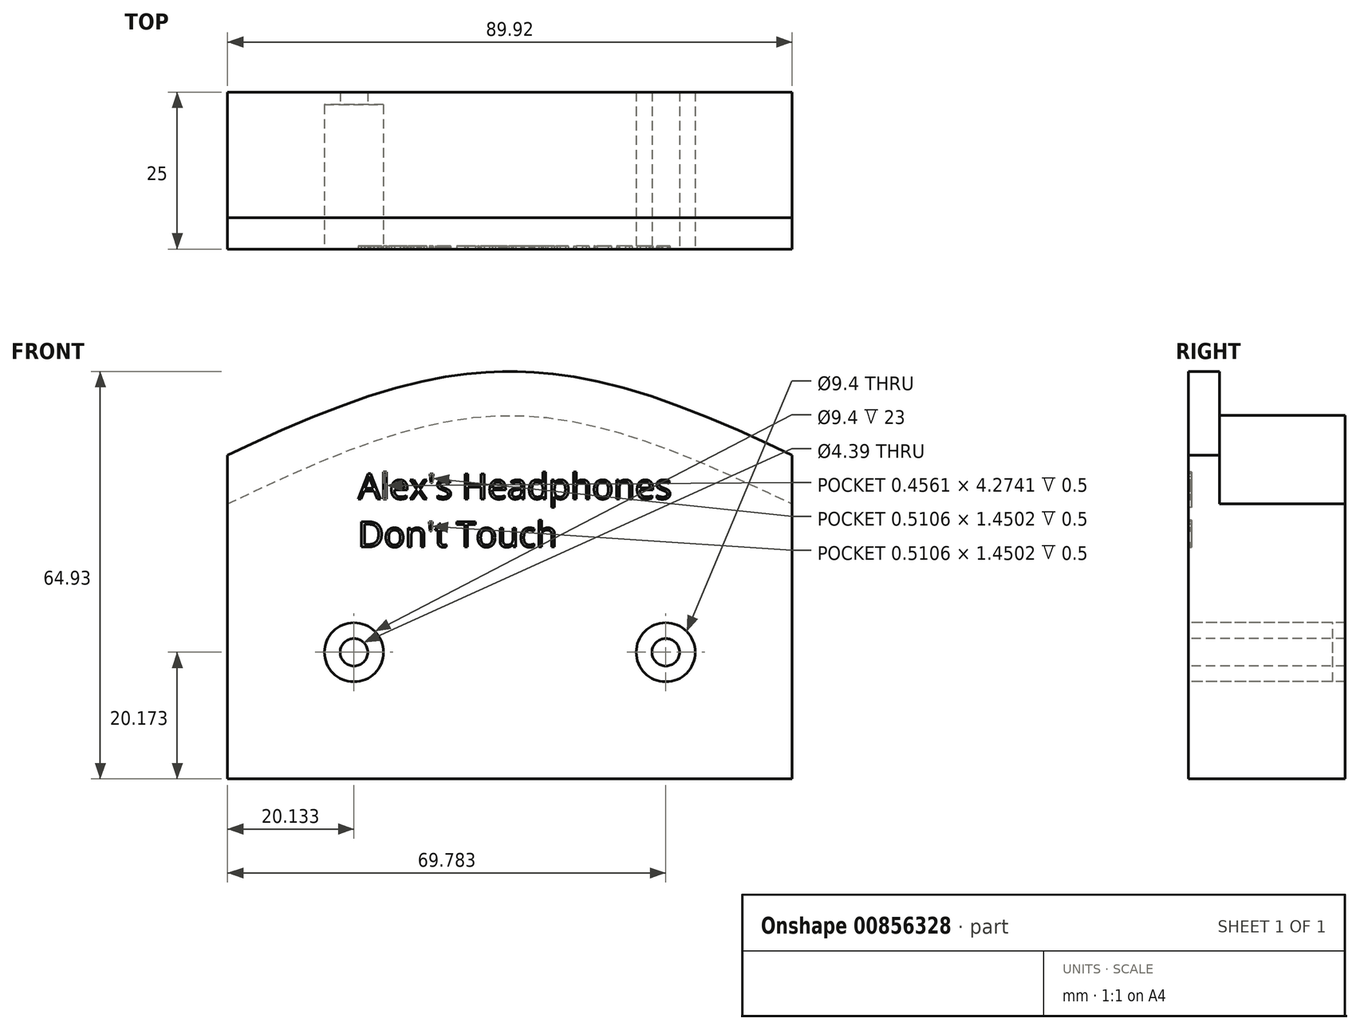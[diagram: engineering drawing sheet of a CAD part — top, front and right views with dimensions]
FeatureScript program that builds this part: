
annotation { "Feature Type Name" : "Feature", "Feature Type Description" : "" }
export const myFeature = defineFeature(function(context is Context, id is Id, definition is map)
    precondition{}
    {
        {
            var Q0;
            Q0=qCreatedBy(makeId("Front.planeOp"),FACE);
            var sketch = newSketch(context, id + "F0", { "sketchPlane" : qUnion([Q0])});
            skLineSegment(sketch, "E0.bottom", {"start": v(0, 0) * mm, "end": v(89.92, 0) * mm});
            skLineSegment(sketch, "E0.top", {"start": v(0, 43.82) * mm, "end": v(89.92, 43.82) * mm});
            skLineSegment(sketch, "E0.left", {"start": v(0, 0) * mm, "end": v(0, 43.82) * mm});
            skLineSegment(sketch, "E0.right", {"start": v(89.92, 0) * mm, "end": v(89.92, 43.82) * mm});
            skPoint(sketch, "E1.1.internal.snap0", {"position": v(44.96, 43.82) * mm});
            skFitSpline(sketch, "E1", {"points": [v(0, 43.82) * mm, v(44.96, 57.92) * mm, v(89.92, 43.82) * mm], "startDerivative": vector(89.92, 42.31) * mm, "endDerivative": vector(89.92, -42.31) * mm});
            skSolve(sketch);
        }
        {
            var Q0;
            Q0=makeQuery(id+"F0.imprint","IMPRINT",FACE,{"disambiguationData":[TD([[makeQuery(id+"F0.imprint","IMPRINT",EDGE,{"derivedFrom":sQuery(id+"F0.wireOp",EDGE,"E0.bottom")}),1.0]])]});
            var Q1;
            Q1=makeQuery(id+"F0.imprint","IMPRINT",FACE,{"disambiguationData":[TD([[makeQuery(id+"F0.imprint","IMPRINT",EDGE,{"derivedFrom":sQuery(id+"F0.wireOp",EDGE,"E0.top")}),1.0]])]});
            extrude(context, id + "F1", {"entities" : qUnion([Q0, Q1]), "depth" : 25 * mm, "offsetDistance" : 25 * mm});
        }
        {
            var Q0;
            Q0=makeQuery(id+"F1.opExtrude","CAP_FACE",FACE,{"disambiguationData":[OSD([sQuery(id+"F0.wireOp",EDGE,"E0.bottom"),sQuery(id+"F0.wireOp",EDGE,"E0.left"),sQuery(id+"F0.wireOp",EDGE,"E0.right"),sQuery(id+"F0.wireOp",EDGE,"E1")])],"isStart":false});
            var sketch = newSketch(context, id + "F2", { "sketchPlane" : qUnion([Q0])});
            skFitSpline(sketch, "E2.0", {"points": [v(-2.98, 50.15) * mm, v(0.77, 51.91) * mm, v(6.46, 54.6) * mm, v(14.22, 57.9) * mm, v(20.13, 60.17) * mm, v(26.15, 62.11) * mm, v(31.26, 63.4) * mm, v(35.42, 64.16) * mm, v(38.57, 64.59) * mm, v(41.22, 64.81) * mm, v(43.35, 64.9) * mm, v(44.96, 64.93) * mm, v(46.57, 64.9) * mm, v(48.7, 64.81) * mm, v(51.35, 64.59) * mm, v(54.5, 64.16) * mm, v(58.65, 63.4) * mm, v(63.77, 62.11) * mm, v(69.78, 60.17) * mm, v(75.7, 57.9) * mm, v(83.46, 54.6) * mm, v(89.15, 51.91) * mm, v(92.9, 50.15) * mm]});
            skLineSegment(sketch, "E3", {"start": v(0, 43.82) * mm, "end": v(0, 51.55) * mm});
            skLineSegment(sketch, "E4", {"start": v(89.92, 43.82) * mm, "end": v(89.92, 51.55) * mm});
            skSolve(sketch);
        }
        {
            var Q0;
            Q0 = qSketchRegion(id + "F2", true);
            var Q1;
            Q1=makeQuery(id+"F2.imprint","IMPRINT",FACE,{"disambiguationData":[TD([[makeQuery(id+"F2.imprint","IMPRINT",EDGE,{"derivedFrom":sQuery(id+"F2.wireOp",EDGE,"E2.0")}),-1.0]])]});
            extrude(context, id + "F3", {"entities" : qUnion([Q0, Q1]), "operationType" : NewBodyOperationType.ADD, "oppositeDirection" : true, "depth" : 5 * mm, "offsetDistance" : 25 * mm});
        }
        {
            var Q0;
            {var subQ0=sQuery(id+"F0.wireOp",EDGE,"E1");Q0=makeQuery(id+"F3.boolean.opBoolean","MERGE",FACE,{"derivedFrom":[makeQuery(id+"F1.opExtrude","CAP_FACE",FACE,{"disambiguationData":[OSD([sQuery(id+"F0.wireOp",EDGE,"E0.bottom"),sQuery(id+"F0.wireOp",EDGE,"E0.left"),sQuery(id+"F0.wireOp",EDGE,"E0.right"),subQ0])],"isStart":false}),makeQuery(id+"F3.opExtrude","CAP_FACE",FACE,{"disambiguationData":[OSD([subQ0,sQuery(id+"F2.wireOp",EDGE,"E2.0"),sQuery(id+"F2.wireOp",EDGE,"E3"),sQuery(id+"F2.wireOp",EDGE,"E4")])],"isStart":true})]});}
            var sketch = newSketch(context, id + "F4", { "sketchPlane" : qUnion([Q0])});
            skCircle(sketch, "E5", {"center": v(20.13, 20.17) * mm, "radius": 4.7 * mm});
            skCircle(sketch, "E6", {"center": v(20.13, 20.17) * mm, "radius": 2.2 * mm});
            skLineSegment(sketch, "E7", {"start": v(44.96, 0) * mm, "end": v(44.96, 64.92) * mm});
            skCircle(sketch, "E8.MirrorC", {"center": v(69.78, 20.17) * mm, "radius": 4.7 * mm});
            skCircle(sketch, "E9.MirrorC", {"center": v(69.78, 20.17) * mm, "radius": 2.2 * mm});
            skSolve(sketch);
        }
        {
            var Q0;
            Q0 = qSketchRegion(id + "F4", true);
            var Q1;
            Q1=makeQuery(id+"F4.imprint","IMPRINT",FACE,{"disambiguationData":[TD([[makeQuery(id+"F4.imprint","IMPRINT",EDGE,{"derivedFrom":sQuery(id+"F4.wireOp",EDGE,"E6")}),1.0]])]});
            extrude(context, id + "F5", {"entities" : qUnion([Q0, Q1]), "operationType" : NewBodyOperationType.REMOVE, "oppositeDirection" : true, "depth" : 23 * mm, "offsetDistance" : 25 * mm});
        }
        {
            var Q0;
            Q0=makeQuery(id+"F4.imprint","IMPRINT",FACE,{"disambiguationData":[TD([[makeQuery(id+"F4.imprint","IMPRINT",EDGE,{"derivedFrom":sQuery(id+"F4.wireOp",EDGE,"E6")}),1.0]])]});
            var Q1;
            Q1=makeQuery(id+"F4.imprint","IMPRINT",FACE,{"disambiguationData":[TD([[makeQuery(id+"F4.imprint","IMPRINT",EDGE,{"derivedFrom":sQuery(id+"F4.wireOp",EDGE,"E9.MirrorC")}),-1.0]])]});
            extrude(context, id + "F6", {"entities" : qUnion([Q0, Q1]), "operationType" : NewBodyOperationType.REMOVE, "oppositeDirection" : true, "depth" : 25 * mm, "offsetDistance" : 25 * mm});
        }
        {
            var Q0;
            {var subQ0=sQuery(id+"F0.wireOp",EDGE,"E0.right");var subQ1=sQuery(id+"F2.wireOp",EDGE,"E3");var subQ2=sQuery(id+"F2.wireOp",EDGE,"E2.0");var subQ3=sQuery(id+"F0.wireOp",EDGE,"E0.left");var subQ4=sQuery(id+"F0.wireOp",EDGE,"E0.bottom");var subQ5=sQuery(id+"F2.wireOp",EDGE,"E4");var subQ6=sQuery(id+"F0.wireOp",EDGE,"E1");Q0=makeQuery(id+"F5.boolean.opBoolean","SPLIT",FACE,{"disambiguationData":[TD([makeQuery(id+"F1.opExtrude","SWEPT_FACE",FACE,{"disambiguationData":[OSD([subQ4])]})])],"derivedFrom":makeQuery(id+"F3.boolean.opBoolean","MERGE",FACE,{"derivedFrom":[makeQuery(id+"F1.opExtrude","CAP_FACE",FACE,{"disambiguationData":[OSD([subQ4,subQ3,subQ0,subQ6])],"isStart":false}),makeQuery(id+"F3.opExtrude","CAP_FACE",FACE,{"disambiguationData":[OSD([subQ6,subQ2,subQ1,subQ5])],"isStart":true})]})});}
            var sketch = newSketch(context, id + "F7", { "sketchPlane" : qUnion([Q0])});
            skText(sketch, "E10", { "text": "Alex\'s Headphones\nDon\'t Touch\n", "fontName": "OpenSans-Regular.ttf"});
            const initialGuessF7  = {"E10": [0.02079, 0.0446, 1, 0, 0.00405]};
            skSetInitialGuess(sketch, initialGuessF7);
            skSolve(sketch);
        }
        {
            var Q0;
            Q0 = qSketchRegion(id + "F7", true);
            extrude(context, id + "F8", {"entities" : qUnion([Q0]), "operationType" : NewBodyOperationType.REMOVE, "endBound" : BoundingType.SYMMETRIC, "oppositeDirection" : true, "depth" : 1 * mm, "offsetDistance" : 25 * mm});
        }
    });
